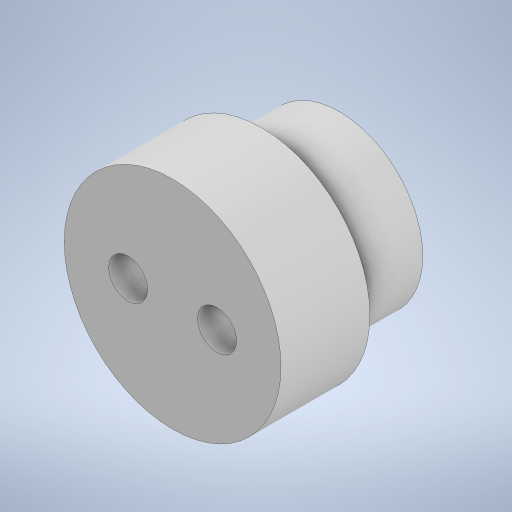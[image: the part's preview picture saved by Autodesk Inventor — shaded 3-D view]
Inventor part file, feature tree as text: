
AUTODESK INVENTOR PART (.ipt)
format: ipt  version: 2023 (Build 270158000, 158)  size: 235,520 bytes
history: native  units: in
note: dims shown in document units (in); Inventor stores cm internally (conversion verified against a paired STEP export)
features: extrude x3, sketch x2, plane x1
ambient origin geometry x8: Origin, YZ Plane, XZ Plane, XY Plane, X Axis, Y Axis, Z Axis, Center Point
bodies: Solid1 (feature_tree)
feature tree (6):
  plane  "Work Plane1"
  sketch  "Sketch1"  dims[d0=0.7677in d1=0.5906in]
  extrude  "Extrusion1"  Depth=0.5906in
  extrude  "Extrusion2"  Depth=0.5906in TaperAngle=0.0deg
  extrude  "Extrusion3"  Depth=0.5906in
  sketch  "Sketch2"  dims[d2=1.0in d3=0.0in d4=0.5906in d5=0.0in d6=0.1378in d7=0.1575in d8=0.315in d9=0.0in d10=0.0in]
